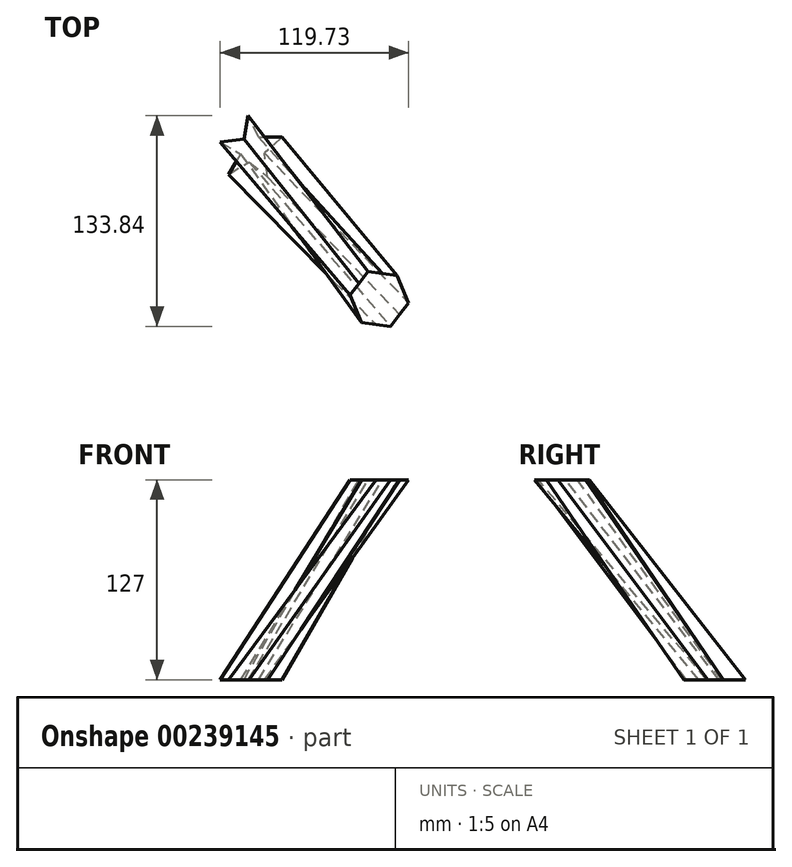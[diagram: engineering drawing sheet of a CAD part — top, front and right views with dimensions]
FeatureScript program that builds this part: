
annotation { "Feature Type Name" : "Feature", "Feature Type Description" : "" }
export const myFeature = defineFeature(function(context is Context, id is Id, definition is map)
    precondition{}
    {
        {
            var Q0;
            Q0=qCreatedBy(makeId("Top.planeOp"),FACE);
            cPlane(context, id + "F0", {"entities" : qUnion([Q0]), "cplaneType" : CPlaneType.OFFSET, "offset" : 127 * mm, "width" : 152.4 * mm, "height" : 152.4 * mm});
        }
        {
            var Q0;
            Q0=qCreatedBy(makeId("Top.planeOp"),FACE);
            var sketch = newSketch(context, id + "F1", { "sketchPlane" : qUnion([Q0])});
            skLineSegment(sketch, "E0", {"start": v(-42, 69.84) * mm, "end": v(-44.8, 54.94) * mm});
            skLineSegment(sketch, "E1", {"start": v(-44.8, 54.94) * mm, "end": v(-59.85, 53.16) * mm});
            skLineSegment(sketch, "E2", {"start": v(-59.85, 53.16) * mm, "end": v(-46.73, 45.56) * mm});
            skLineSegment(sketch, "E3", {"start": v(-46.73, 45.56) * mm, "end": v(-54.33, 32.44) * mm});
            skLineSegment(sketch, "E4", {"start": v(-54.33, 32.44) * mm, "end": v(-41.5, 40.52) * mm});
            skLineSegment(sketch, "E5", {"start": v(-41.5, 40.52) * mm, "end": v(-29.76, 30.94) * mm});
            skLineSegment(sketch, "E6", {"start": v(-29.76, 30.94) * mm, "end": v(-31.69, 45.98) * mm});
            skLineSegment(sketch, "E7", {"start": v(-35.57, 56.11) * mm, "end": v(-42, 69.84) * mm});
            skLineSegment(sketch, "E8", {"start": v(-35.57, 56.11) * mm, "end": v(-20.41, 56.11) * mm});
            skLineSegment(sketch, "E9", {"start": v(-20.41, 56.11) * mm, "end": v(-31.69, 45.98) * mm});
            skSolve(sketch);
        }
        {
            var Q0;
            Q0=qCreatedBy(id+"F0.planeOp",FACE);
            var sketch = newSketch(context, id + "F2", { "sketchPlane" : qUnion([Q0])});
            skCircle(sketch, "E10.cCircle", {"center": v(41.23, -46.64) * mm, "radius": 16.29 * mm, "construction": true});
            skLineSegment(sketch, "E10.0", {"start": v(59.88, -49.05) * mm, "end": v(48.46, -64) * mm});
            skLineSegment(sketch, "E10.1", {"start": v(48.46, -64) * mm, "end": v(29.81, -61.58) * mm});
            skLineSegment(sketch, "E10.2", {"start": v(29.81, -61.58) * mm, "end": v(22.58, -44.23) * mm});
            skLineSegment(sketch, "E10.3", {"start": v(22.58, -44.23) * mm, "end": v(34, -29.28) * mm});
            skLineSegment(sketch, "E10.4", {"start": v(34, -29.28) * mm, "end": v(52.64, -31.7) * mm});
            skLineSegment(sketch, "E10.5", {"start": v(52.64, -31.7) * mm, "end": v(59.88, -49.05) * mm});
            skPoint(sketch, "E10.0.midPoint", {"position": v(54.17, -56.53) * mm});
            skSolve(sketch);
        }
        {
            var Q0;
            Q0 = qSketchRegion(id + "F1", true);
            var Q1;
            Q1 = qSketchRegion(id + "F2", true);
            loft(context, id + "F3", {"sheetProfilesArray" : [{ "sheetProfileEntities" : qUnion([Q0]) }, { "sheetProfileEntities" : qUnion([Q1]) }]});
        }
    });
